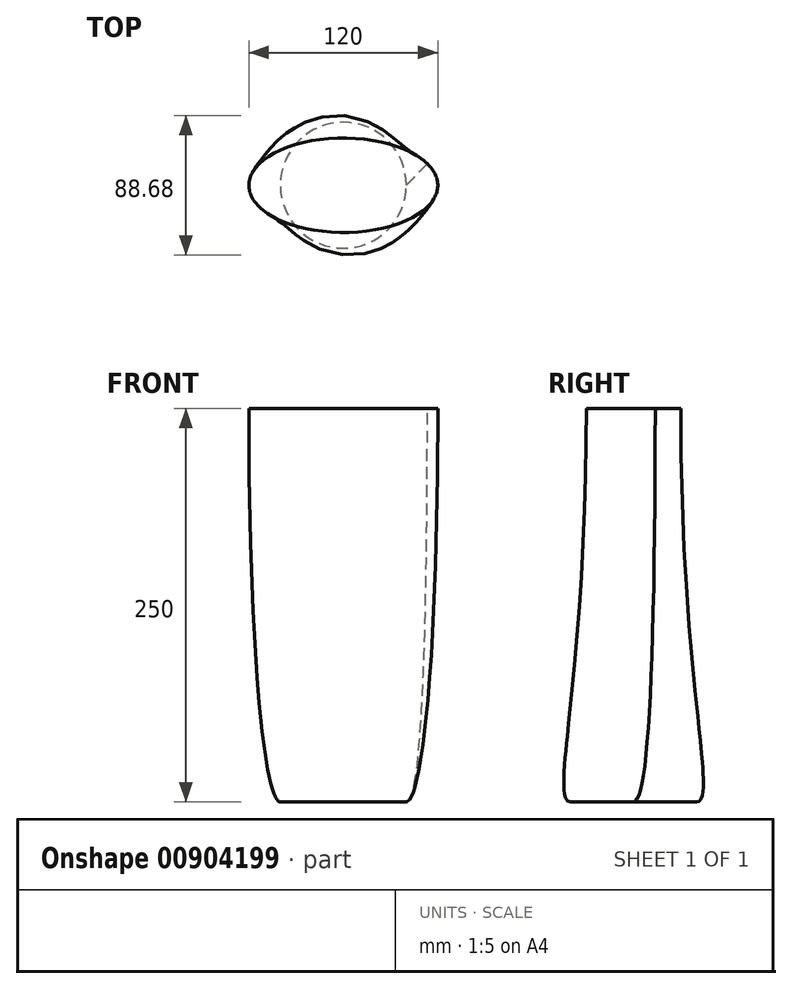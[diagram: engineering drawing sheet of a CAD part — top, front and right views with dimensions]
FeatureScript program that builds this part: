
annotation { "Feature Type Name" : "Feature", "Feature Type Description" : "" }
export const myFeature = defineFeature(function(context is Context, id is Id, definition is map)
    precondition{}
    {
        {
            var Q0;
            Q0=qCreatedBy(makeId("Top.planeOp"),FACE);
            var sketch = newSketch(context, id + "F0", { "sketchPlane" : qUnion([Q0])});
            skCircle(sketch, "E0", {"center": v(0, 0) * mm, "radius": 40 * mm});
            skSolve(sketch);
        }
        {
            var Q0;
            Q0=qCreatedBy(makeId("Top.planeOp"),FACE);
            cPlane(context, id + "F1", {"entities" : qUnion([Q0]), "cplaneType" : CPlaneType.OFFSET, "offset" : 250 * mm, "width" : 150 * mm, "height" : 150 * mm});
        }
        {
            var Q0;
            Q0=qCreatedBy(id+"F1.planeOp",FACE);
            var sketch = newSketch(context, id + "F2", { "sketchPlane" : qUnion([Q0])});
            skEllipse(sketch, "E1", {"center": v(0, 0) * mm, "majorRadius": 60 * mm, "minorRadius": 30 * mm, "majorAxis": v(1, 0)});
            skSolve(sketch);
        }
        {
            var Q0;
            Q0=makeQuery(id+"F0.imprint","IMPRINT",FACE,{"disambiguationData":[TD([[makeQuery(id+"F0.imprint","IMPRINT",EDGE,{"derivedFrom":sQuery(id+"F0.wireOp",EDGE,"E0")}),1.0]])]});
            var Q1;
            Q1=makeQuery(id+"F2.imprint","IMPRINT",FACE,{"disambiguationData":[TD([[makeQuery(id+"F2.imprint","IMPRINT",EDGE,{"derivedFrom":sQuery(id+"F2.wireOp",EDGE,"E1")}),1.0]])]});
            loft(context, id + "F3", {"startCondition" : LoftEndDerivativeType.TANGENT_TO_PROFILE, "startMagnitude" : 2, "endCondition" : LoftEndDerivativeType.NORMAL_TO_PROFILE, "endMagnitude" : 2, "sheetProfilesArray" : [{ "sheetProfileEntities" : qUnion([Q0]) }, { "sheetProfileEntities" : qUnion([Q1]) }]});
        }
    });
